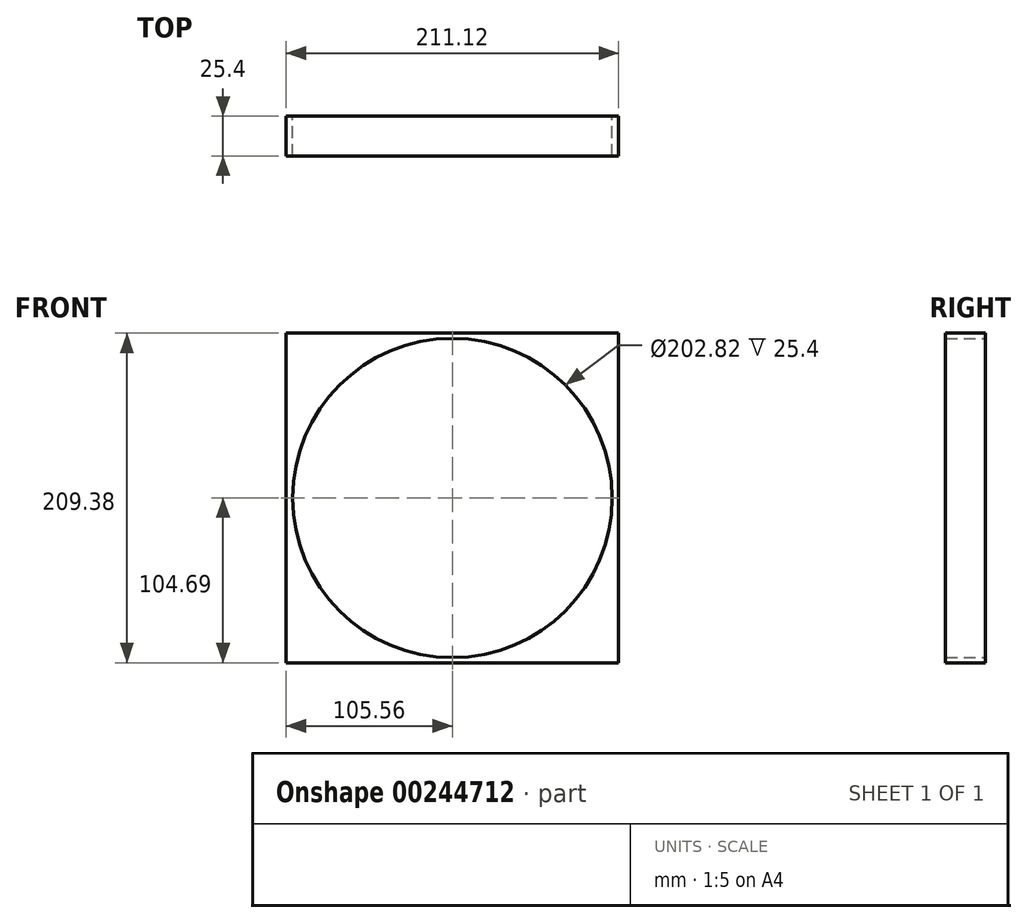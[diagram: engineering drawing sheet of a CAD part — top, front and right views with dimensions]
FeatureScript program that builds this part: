
annotation { "Feature Type Name" : "Feature", "Feature Type Description" : "" }
export const myFeature = defineFeature(function(context is Context, id is Id, definition is map)
    precondition{}
    {
        {
            var Q0;
            Q0=qCreatedBy(makeId("Front.planeOp"),FACE);
            var sketch = newSketch(context, id + "F0", { "sketchPlane" : qUnion([Q0])});
            skLineSegment(sketch, "E0.bottom", {"start": v(-105.56, 104.7) * mm, "end": v(105.56, 104.7) * mm});
            skLineSegment(sketch, "E0.top", {"start": v(-105.56, -104.7) * mm, "end": v(105.56, -104.7) * mm});
            skLineSegment(sketch, "E0.left", {"start": v(-105.56, 104.7) * mm, "end": v(-105.56, -104.7) * mm});
            skLineSegment(sketch, "E0.right", {"start": v(105.56, 104.7) * mm, "end": v(105.56, -104.7) * mm});
            skPoint(sketch, "E0.middle", {"position": v(0, 0) * mm});
            skCircle(sketch, "E1", {"center": v(0, 0) * mm, "radius": 76.17 * mm});
            skCircle(sketch, "E2", {"center": v(0, 0) * mm, "radius": 89.23 * mm});
            skCircle(sketch, "E3", {"center": v(0, 0) * mm, "radius": 101.41 * mm});
            skSolve(sketch);
        }
        {
            var Q0;
            Q0=makeQuery(id+"F0.imprint","IMPRINT",FACE,{"disambiguationData":[TD([[makeQuery(id+"F0.imprint","IMPRINT",EDGE,{"derivedFrom":sQuery(id+"F0.wireOp",EDGE,"E0.bottom")}),-1.0]])]});
            extrude(context, id + "F1", {"entities" : qUnion([Q0]), "depth" : 25.4 * mm});
        }
        {
            var Q0;
            Q0 = qSketchRegion(id + "F0", true);
            extrude(context, id + "F2", {"entities" : qUnion([Q0]), "operationType" : NewBodyOperationType.ADD, "depth" : 25.4 * mm});
        }
    });
